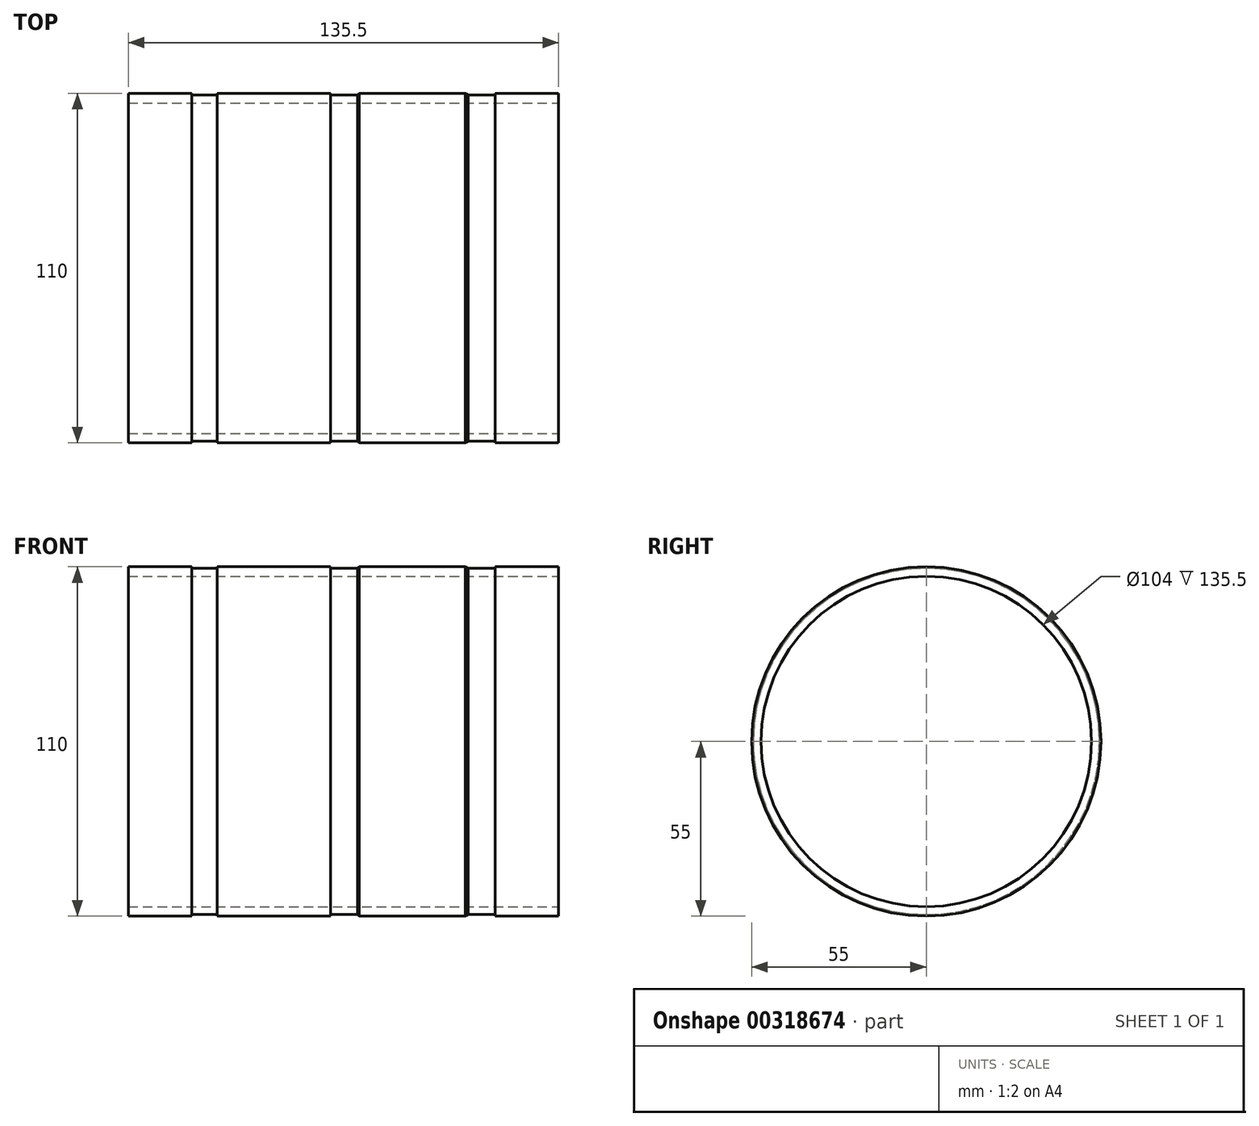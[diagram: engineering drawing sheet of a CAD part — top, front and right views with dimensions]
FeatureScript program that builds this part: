
annotation { "Feature Type Name" : "Feature", "Feature Type Description" : "" }
export const myFeature = defineFeature(function(context is Context, id is Id, definition is map)
    precondition{}
    {
        {
            var Q0;
            Q0=qCreatedBy(makeId("Front.planeOp"),FACE);
            var sketch = newSketch(context, id + "F0", { "sketchPlane" : qUnion([Q0])});
            skLineSegment(sketch, "E0", {"start": v(-84.26, 55) * mm, "end": v(-64.26, 55) * mm});
            skLineSegment(sketch, "E1", {"start": v(-64.26, 55) * mm, "end": v(-64.26, 54.5) * mm});
            skLineSegment(sketch, "E2", {"start": v(-64.26, 54.5) * mm, "end": v(-56.26, 54.5) * mm});
            skLineSegment(sketch, "E3", {"start": v(-56.26, 54.5) * mm, "end": v(-56.26, 55) * mm});
            skLineSegment(sketch, "E4", {"start": v(-56.26, 55) * mm, "end": v(-20.51, 55) * mm});
            skLineSegment(sketch, "E5", {"start": v(-20.51, 55) * mm, "end": v(-20.51, 54.5) * mm});
            skLineSegment(sketch, "E6", {"start": v(-20.51, 54.5) * mm, "end": v(-12.51, 54.5) * mm});
            skLineSegment(sketch, "E7", {"start": v(-12.51, 54.5) * mm, "end": v(-12.51, 55) * mm});
            skLineSegment(sketch, "E8", {"start": v(-12.51, 55) * mm, "end": v(23.24, 55) * mm});
            skLineSegment(sketch, "E9", {"start": v(23.24, 55) * mm, "end": v(23.24, 54.5) * mm});
            skLineSegment(sketch, "E10", {"start": v(23.24, 54.5) * mm, "end": v(31.24, 54.5) * mm});
            skLineSegment(sketch, "E11", {"start": v(31.24, 54.5) * mm, "end": v(31.24, 55) * mm});
            skLineSegment(sketch, "E12", {"start": v(31.24, 55) * mm, "end": v(51.24, 55) * mm});
            skLineSegment(sketch, "E13", {"start": v(51.24, 55) * mm, "end": v(51.24, 52) * mm});
            skLineSegment(sketch, "E14", {"start": v(51.24, 52) * mm, "end": v(-84.26, 52) * mm});
            skLineSegment(sketch, "E15", {"start": v(-84.26, 52) * mm, "end": v(-84.26, 55) * mm});
            skLineSegment(sketch, "E16", {"start": v(49.08, 0) * mm, "end": v(-60.95, 0) * mm});
            skSolve(sketch);
        }
        {
            var Q0;
            Q0=makeQuery(id+"F0.imprint","IMPRINT",FACE,{"disambiguationData":[TD([[makeQuery(id+"F0.imprint","IMPRINT",EDGE,{"derivedFrom":sQuery(id+"F0.wireOp",EDGE,"E0")}),-1.0]])]});
            var Q1;
            Q1=sQuery(id+"F0.wireOp",EDGE,"E16");
            revolve(context, id + "F1", {"entities" : qUnion([Q0]), "axis" : qUnion([Q1]), "revolveType" : RevolveType.FULL});
        }
        {
            var Q0;
            Q0=makeQuery(id+"F1.opRevolve","SWEPT_FACE",FACE,{"disambiguationData":[OSD([sQuery(id+"F0.wireOp",EDGE,"E8")])]});
            chamfer(context, id + "F2", {"entities" : qUnion([Q0]), "width" : 1 * mm, "tangentPropagation" : true});
        }
        {
            var Q0;
            {var subQ0=sQuery(id+"F0.wireOp",EDGE,"E8");Q0=makeQuery(id+"F2.opChamfer","BLEND_EDGE",EDGE,{"blendedFrom":[makeQuery(id+"F1.opRevolve","SWEPT_EDGE",EDGE,{"disambiguationData":[OSD([subQ0,sQuery(id+"F0.wireOp",EDGE,"E9")])]}),makeQuery(id+"F1.opRevolve","SWEPT_FACE",FACE,{"disambiguationData":[OSD([subQ0])]})],"blendedInto":[makeQuery(id+"F1.opRevolve","SWEPT_FACE",FACE,{"disambiguationData":[OSD([subQ0])]})]});}
            chamfer(context, id + "F3", {"entities" : qUnion([Q0]), "width" : 1 * mm, "tangentPropagation" : true});
        }
    });
